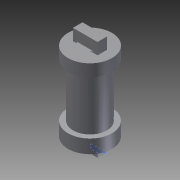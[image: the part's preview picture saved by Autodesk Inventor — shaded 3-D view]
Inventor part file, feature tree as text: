
AUTODESK INVENTOR PART (.ipt)
format: ipt  version: 2012 (Build 160160000, 160)  size: 172,032 bytes
history: native  units: mm
features: extrude x11, sketch x11, projected_geometry x4, reference x1
ambient origin geometry x8: Origin, YZ Plane, XZ Plane, XY Plane, X Axis, Y Axis, Z Axis, Center Point
bodies: Solid1 (feature_tree)
feature tree (27):
  extrude  "Extrusion1"  Depth=2.0mm TaperAngle=0.0deg
  extrude  "Extrusion2"  Depth=2.0mm TaperAngle=0.0deg
  extrude  "Extrusion3"  Depth=4.909mm
  extrude  "Extrusion4"  Depth=1.909188mm
  extrude  "Extrusion5"  Depth=2.0mm
  extrude  "Extrusion6"  Depth=10.0mm TaperAngle=0.0deg
  extrude  "Extrusion7"  Depth=2.7mm
  extrude  "Extrusion8"  Depth=10.0mm TaperAngle=0.0deg
  extrude  "Extrusion9"  Depth=10.0mm TaperAngle=0.0deg
  extrude  "Extrusion11"  Depth=0.3mm TaperAngle=0.0deg
  extrude  "Extrusion12"  [1 undecoded]
  sketch  "Sketch1"  dims[d1=5.0mm d2=15.0mm d3=0.0mm d4=0.0mm d5=2.0mm d6=0.0mm]
  reference  "Reference1"
  sketch  "Sketch2"  dims[d7=2.7mm d8=0.0mm d9=2.0mm d10=0.0mm]
  projected_geometry  "Projected Loop1"
  sketch  "Sketch3"  dims[d11=2.7mm d12=0.0mm d13=4.909mm]
  projected_geometry  "Projected Loop2"
  sketch  "Sketch4"  dims[d14=1.499906mm d15=1.909188mm]
  projected_geometry  "Projected Loop3"
  projected_geometry  "Projected Loop4"
  sketch  "Sketch5"  dims[d16=2.0mm d17=2.0mm]
  sketch  "Sketch7"  dims[d18=0.0mm d19=10.0mm d20=0.0mm]
  sketch  "Sketch8"  dims[d21=2.7mm d22=2.7mm]
  sketch  "Sketch9"  dims[d23=6.75mm d24=10.0mm d25=0.0mm]
  sketch  "Sketch10"  dims[d26=1.0mm d27=10.0mm d28=0.0mm]
  sketch  "Sketch12"  dims[d29=10.0mm d30=0.0mm d33=0.3mm d34=0.0mm]
  sketch  "Sketch13"  dims[d35=0.3mm d36=0.0mm]
note: 1 required parameter value undecoded (feature->parameter linkage not recoverable at this tier; creation-order binding heuristic only, values carry confidence <= 0.55)
